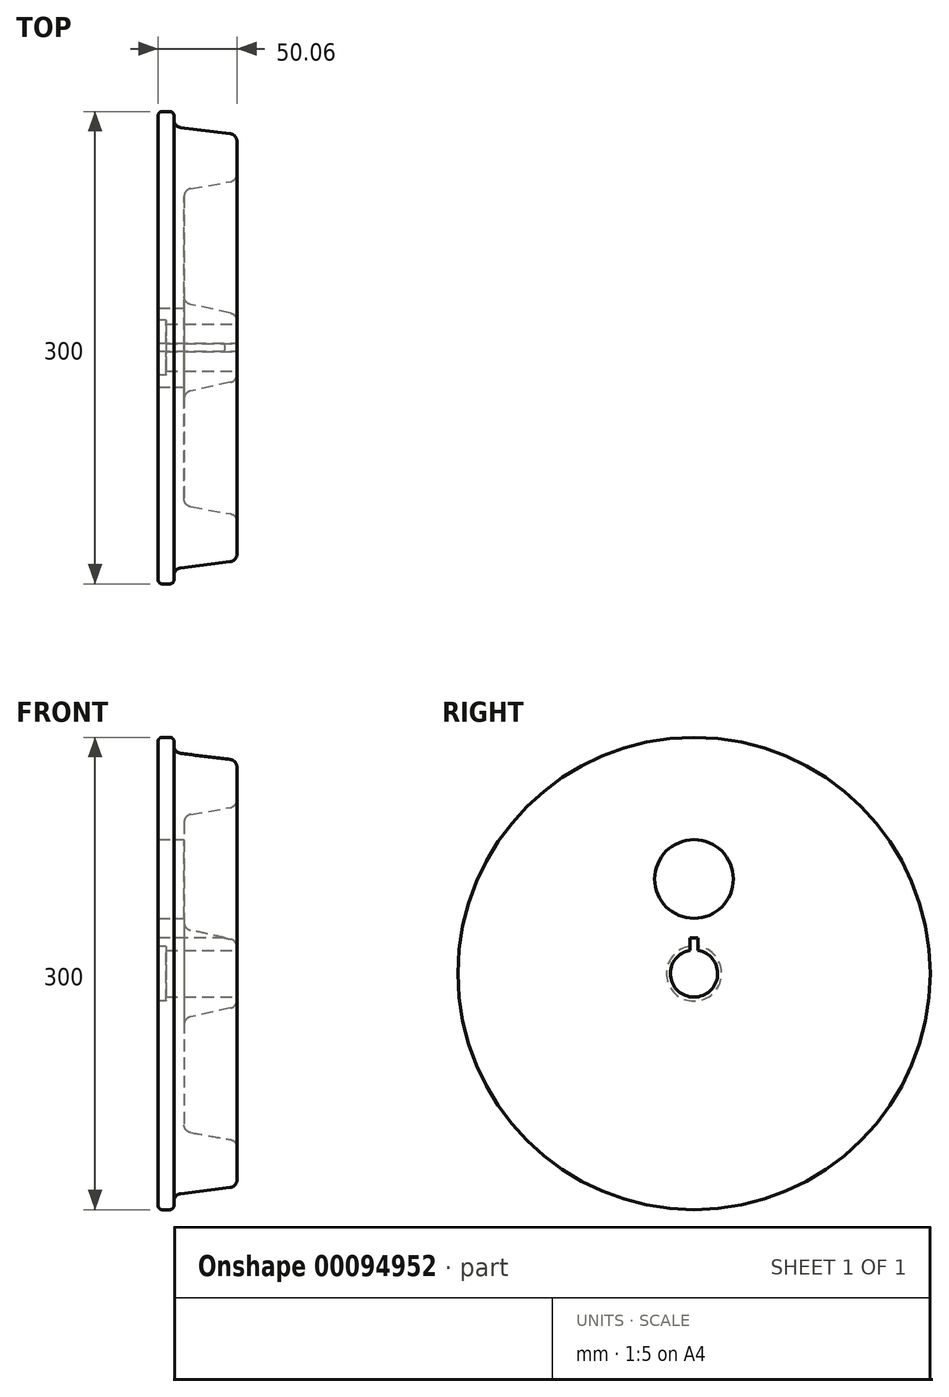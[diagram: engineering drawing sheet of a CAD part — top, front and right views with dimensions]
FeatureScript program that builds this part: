
annotation { "Feature Type Name" : "Feature", "Feature Type Description" : "" }
export const myFeature = defineFeature(function(context is Context, id is Id, definition is map)
    precondition{}
    {
        {
            var Q0;
            Q0=qCreatedBy(makeId("Top.planeOp"),FACE);
            var sketch = newSketch(context, id + "F0", { "sketchPlane" : qUnion([Q0])});
            skLineSegment(sketch, "E0", {"start": v(0, 0) * mm, "end": v(0, 150) * mm});
            skLineSegment(sketch, "E1", {"start": v(0, 150) * mm, "end": v(10, 150) * mm});
            skLineSegment(sketch, "E2", {"start": v(10, 150) * mm, "end": v(10, 140.35) * mm});
            skLineSegment(sketch, "E3", {"start": v(10, 140.35) * mm, "end": v(50.06, 135.43) * mm});
            skLineSegment(sketch, "E4", {"start": v(50, 0) * mm, "end": v(0, 0) * mm});
            skLineSegment(sketch, "E5", {"start": v(50.06, 135.43) * mm, "end": v(50.06, 106.2) * mm});
            skLineSegment(sketch, "E6", {"start": v(50.06, 106.2) * mm, "end": v(16.5, 100.29) * mm});
            skLineSegment(sketch, "E7", {"start": v(16.5, 100.29) * mm, "end": v(16.5, 28.4) * mm});
            skLineSegment(sketch, "E8", {"start": v(16.5, 28.4) * mm, "end": v(50, 21.05) * mm});
            skLineSegment(sketch, "E9", {"start": v(50, 21.05) * mm, "end": v(50, 0) * mm});
            skSolve(sketch);
        }
        {
            var Q0;
            Q0=makeQuery(id+"F0.imprint","IMPRINT",FACE,{"disambiguationData":[TD([[makeQuery(id+"F0.imprint","IMPRINT",EDGE,{"derivedFrom":sQuery(id+"F0.wireOp",EDGE,"E0")}),-1.0]])]});
            var Q1;
            Q1=sQuery(id+"F0.wireOp",EDGE,"E4");
            revolve(context, id + "F1", {"entities" : qUnion([Q0]), "axis" : qUnion([Q1]), "revolveType" : RevolveType.FULL});
        }
        {
            var Q0;
            Q0=makeQuery(id+"F1.opRevolve","SWEPT_FACE",FACE,{"disambiguationData":[OSD([sQuery(id+"F0.wireOp",EDGE,"E9")])]});
            var sketch = newSketch(context, id + "F2", { "sketchPlane" : qUnion([Q0])});
            skPoint(sketch, "E10", {"position": v(0, 0) * mm});
            skCircle(sketch, "E11", {"center": v(0, 0) * mm, "radius": 15 * mm});
            skSolve(sketch);
        }
        {
            var Q0;
            Q0=makeQuery(id+"F2.imprint","IMPRINT",FACE,{"disambiguationData":[TD([[makeQuery(id+"F2.imprint","IMPRINT",EDGE,{"derivedFrom":sQuery(id+"F2.wireOp",EDGE,"E11")}),1.0]])]});
            var Q1;
            Q1=sQuery(id+"F2.wireOp",EDGE,"E11");
            extrude(context, id + "F3", {"entities" : qUnion([Q0]), "operationType" : NewBodyOperationType.REMOVE, "surfaceEntities" : qUnion([Q1]), "endBound" : BoundingType.UP_TO_NEXT, "oppositeDirection" : true, "depth" : 25 * mm});
        }
        {
            var Q0;
            Q0=makeQuery(id+"F1.opRevolve","SWEPT_FACE",FACE,{"disambiguationData":[OSD([sQuery(id+"F0.wireOp",EDGE,"E7")])]});
            var sketch = newSketch(context, id + "F4", { "sketchPlane" : qUnion([Q0])});
            skCircle(sketch, "E12", {"center": v(0, 60) * mm, "radius": 25 * mm});
            skSolve(sketch);
        }
        {
            var Q0;
            Q0=makeQuery(id+"F4.imprint","IMPRINT",FACE,{"disambiguationData":[TD([[makeQuery(id+"F4.imprint","IMPRINT",EDGE,{"derivedFrom":sQuery(id+"F4.wireOp",EDGE,"E12")}),1.0]])]});
            extrude(context, id + "F5", {"entities" : qUnion([Q0]), "operationType" : NewBodyOperationType.REMOVE, "endBound" : BoundingType.UP_TO_NEXT, "oppositeDirection" : true, "depth" : 25 * mm});
        }
        {
            var Q0;
            Q0=makeQuery(id+"F1.opRevolve","SWEPT_FACE",FACE,{"disambiguationData":[OSD([sQuery(id+"F0.wireOp",EDGE,"E0")])]});
            var sketch = newSketch(context, id + "F6", { "sketchPlane" : qUnion([Q0])});
            skCircle(sketch, "E13", {"center": v(0, 0) * mm, "radius": 17.5 * mm});
            skSolve(sketch);
        }
        {
            var Q0;
            Q0 = qSketchRegion(id + "F6", true);
            extrude(context, id + "F7", {"entities" : qUnion([Q0]), "operationType" : NewBodyOperationType.REMOVE, "oppositeDirection" : true, "depth" : 5 * mm});
        }
        {
            var Q0;
            Q0=makeQuery(id+"F1.opRevolve","SWEPT_EDGE",EDGE,{"disambiguationData":[OSD([sQuery(id+"F0.wireOp",EDGE,"E6"),sQuery(id+"F0.wireOp",EDGE,"E7")])]});
            var Q1;
            Q1=makeQuery(id+"F1.opRevolve","SWEPT_FACE",FACE,{"disambiguationData":[OSD([sQuery(id+"F0.wireOp",EDGE,"E5")])]});
            var Q2;
            Q2=makeQuery(id+"F1.opRevolve","SWEPT_EDGE",EDGE,{"disambiguationData":[OSD([sQuery(id+"F0.wireOp",EDGE,"E2"),sQuery(id+"F0.wireOp",EDGE,"E3")])]});
            var Q3;
            Q3=makeQuery(id+"F1.opRevolve","SWEPT_EDGE",EDGE,{"disambiguationData":[OSD([sQuery(id+"F0.wireOp",EDGE,"E8"),sQuery(id+"F0.wireOp",EDGE,"E9")])]});
            var Q4;
            Q4=makeQuery(id+"F1.opRevolve","SWEPT_EDGE",EDGE,{"disambiguationData":[OSD([sQuery(id+"F0.wireOp",EDGE,"E7"),sQuery(id+"F0.wireOp",EDGE,"E8")])]});
            fillet(context, id + "F8", {"entities" : qUnion([Q0, Q1, Q2, Q3, Q4]), "radius" : 5 * mm, "tangentPropagation" : true, "allowEdgeOverflow" : false});
        }
        {
            var Q0;
            Q0=makeQuery(id+"F1.opRevolve","SWEPT_EDGE",EDGE,{"disambiguationData":[OSD([sQuery(id+"F0.wireOp",EDGE,"E1"),sQuery(id+"F0.wireOp",EDGE,"E2")])]});
            var Q1;
            Q1=makeQuery(id+"F1.opRevolve","SWEPT_EDGE",EDGE,{"disambiguationData":[OSD([sQuery(id+"F0.wireOp",EDGE,"E0"),sQuery(id+"F0.wireOp",EDGE,"E1")])]});
            fillet(context, id + "F9", {"entities" : qUnion([Q0, Q1]), "radius" : 2.5 * mm, "tangentPropagation" : true, "allowEdgeOverflow" : false});
        }
        {
            var Q0;
            Q0=makeQuery(id+"F1.opRevolve","SWEPT_FACE",FACE,{"disambiguationData":[OSD([sQuery(id+"F0.wireOp",EDGE,"E0")])]});
            var sketch = newSketch(context, id + "F10", { "sketchPlane" : qUnion([Q0])});
            skLineSegment(sketch, "E14.bottom", {"start": v(-2.5, 13.1) * mm, "end": v(2.5, 13.1) * mm});
            skLineSegment(sketch, "E14.top", {"start": v(-2.5, 22.68) * mm, "end": v(2.5, 22.68) * mm});
            skLineSegment(sketch, "E14.left", {"start": v(-2.5, 13.1) * mm, "end": v(-2.5, 22.68) * mm});
            skLineSegment(sketch, "E14.right", {"start": v(2.5, 13.1) * mm, "end": v(2.5, 22.68) * mm});
            skLineSegment(sketch, "E15", {"start": v(0, 0) * mm, "end": v(0, 29.02) * mm, "construction": true});
            skSolve(sketch);
        }
        {
            var Q0;
            Q0 = qSketchRegion(id + "F10", true);
            extrude(context, id + "F11", {"entities" : qUnion([Q0]), "operationType" : NewBodyOperationType.REMOVE, "endBound" : BoundingType.UP_TO_NEXT, "oppositeDirection" : true, "depth" : 25 * mm});
        }
    });
